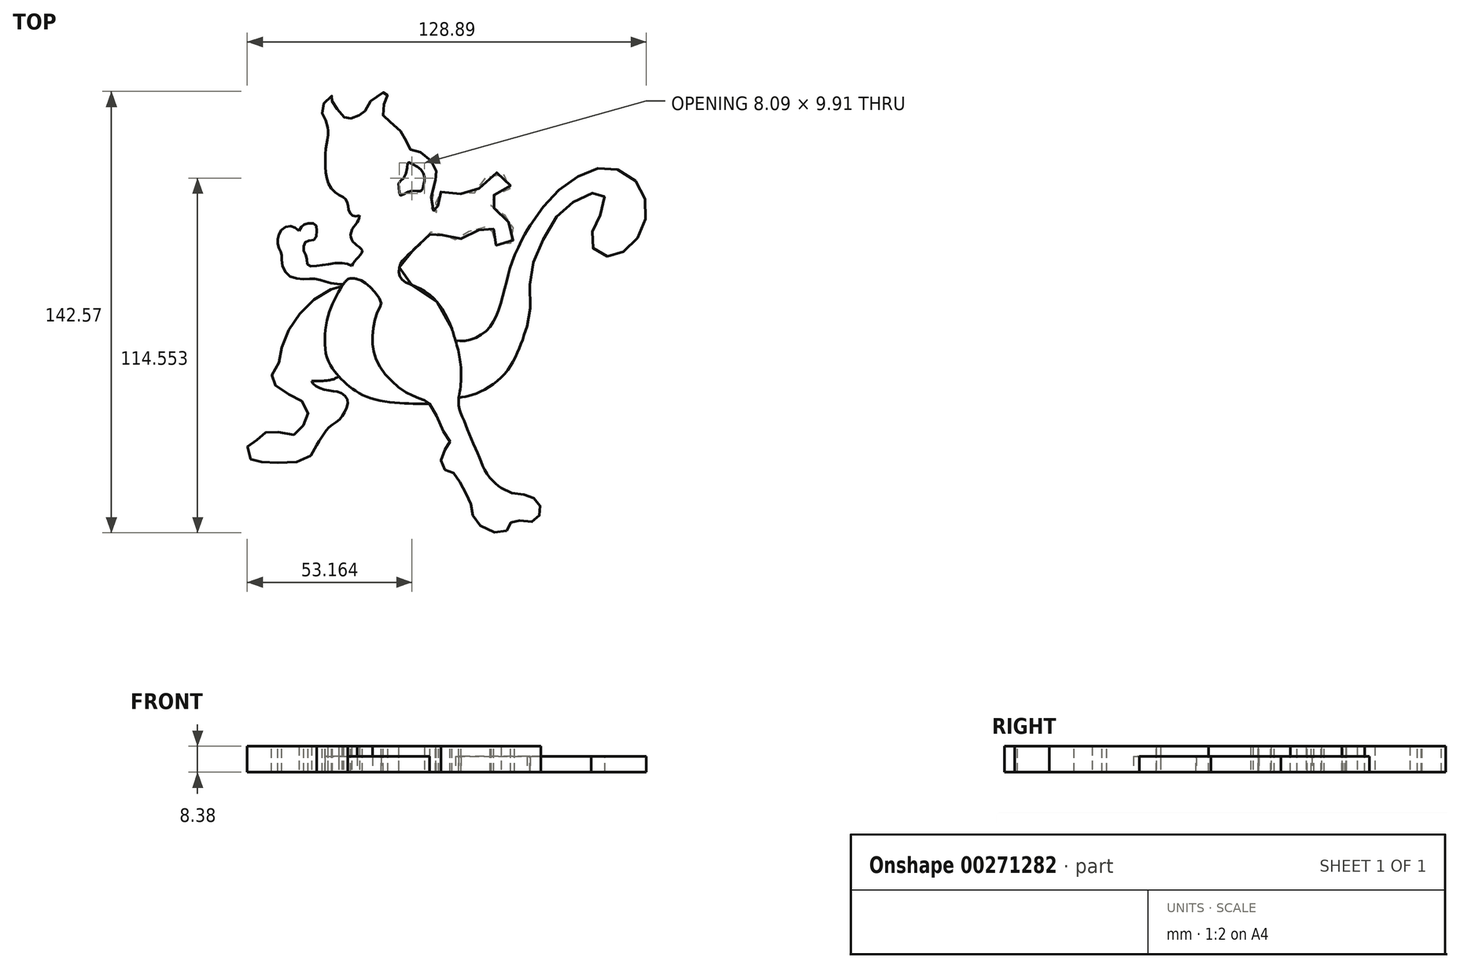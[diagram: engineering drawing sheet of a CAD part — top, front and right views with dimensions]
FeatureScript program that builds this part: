
annotation { "Feature Type Name" : "Feature", "Feature Type Description" : "" }
export const myFeature = defineFeature(function(context is Context, id is Id, definition is map)
    precondition{}
    {
        {
            var Q0;
            Q0=qCreatedBy(makeId("Top.planeOp"),FACE);
            var sketch = newSketch(context, id + "F0", { "sketchPlane" : qUnion([Q0])});
            skFitSpline(sketch, "E0", {"points": [v(-30.68, 33.26) * mm, v(-32.55, 33.12) * mm, v(-33.7, 33.93) * mm, v(-34.3, 35.74) * mm, v(-34.5, 37.15) * mm, v(-35.3, 38.69) * mm, v(-36.98, 39.76) * mm, v(-39.6, 41.77) * mm, v(-41.27, 45.4) * mm, v(-41.74, 50.1) * mm, v(-41.68, 54.72) * mm, v(-41.14, 57.2) * mm, v(-40.87, 60.29) * mm, v(-41, 61.76) * mm], "startDerivative": vector(-29.89, -5.6) * mm, "endDerivative": vector(-3.16, 22.04) * mm});
            skFitSpline(sketch, "E1", {"points": [v(-41, 61.76) * mm, v(-41.17, 62.73) * mm, v(-41.87, 64.35) * mm, v(-42.58, 65.62) * mm, v(-42.68, 67.95) * mm, v(-41.66, 70.39) * mm, v(-39.53, 72) * mm, v(-39.68, 71.35) * mm, v(-39.43, 69.88) * mm, v(-38.31, 68.15) * mm, v(-36.34, 65.92) * mm, v(-34.76, 64.3) * mm, v(-33.44, 64.8) * mm, v(-31.72, 65.72) * mm, v(-29.44, 65.67) * mm, v(-28.78, 68.05) * mm, v(-26.24, 71) * mm, v(-21.98, 73.38) * mm, v(-21.52, 72.72) * mm, v(-22.49, 70.8) * mm, v(-22.9, 68) * mm, v(-22.94, 65.21) * mm, v(-20.91, 63.69) * mm, v(-17.41, 60.44) * mm, v(-15.59, 57.5) * mm, v(-14.77, 54.91) * mm, v(-13, 54.5) * mm, v(-9.24, 52.68) * mm, v(-6.56, 49.33) * mm, v(-5.9, 46.64) * mm, v(-6.17, 44.77) * mm], "startDerivative": vector(-4.63, 41.75) * mm, "endDerivative": vector(1.78, -61.04) * mm});
            skFitSpline(sketch, "E2", {"points": [v(-10.86, 41.22) * mm, v(-13.35, 41.27) * mm, v(-15.9, 40.53) * mm, v(-17.55, 39.84) * mm, v(-17.97, 41.87) * mm, v(-17.97, 43.9) * mm, v(-16.72, 45.15) * mm, v(-15.38, 48.56) * mm, v(-15.06, 50.5) * mm, v(-13.44, 49.9) * mm, v(-11.09, 48.29) * mm, v(-9.93, 46.35) * mm, v(-9.75, 44.36) * mm, v(-10.12, 42.65) * mm, v(-10.86, 41.22) * mm]});
            skFitSpline(sketch, "E3", {"points": [v(-6.17, 44.77) * mm, v(-6.16, 41.94) * mm, v(-6.95, 40.05) * mm, v(-7.82, 38.74) * mm, v(-7.9, 37.04) * mm, v(-7.54, 35.26) * mm, v(-6.56, 34.7) * mm, v(-6.17, 34.08) * mm, v(-5.4, 34.9) * mm, v(-5.12, 35.69) * mm, v(-5.55, 36.6) * mm, v(-6.17, 38.2) * mm, v(-5.6, 39.95) * mm, v(-3.84, 41.22) * mm, v(-1.16, 41.22) * mm, v(1.86, 40.31) * mm, v(4.7, 40.3) * mm, v(7.28, 41.22) * mm, v(9.35, 44.77) * mm, v(12.66, 47.12) * mm, v(15.97, 46.6) * mm, v(17.73, 44.77) * mm, v(17.63, 41.22) * mm, v(15.25, 39.88) * mm, v(12.14, 39.78) * mm, v(11.52, 38.23) * mm, v(11.73, 36.57) * mm, v(13.7, 35.12) * mm, v(16.28, 33.26) * mm, v(17.63, 30.99) * mm, v(18.97, 29.02) * mm, v(19.18, 25.92) * mm, v(17.52, 23.95) * mm, v(15.56, 23.23) * mm, v(12.87, 24.06) * mm, v(11.83, 26.44) * mm, v(12.35, 28.4) * mm, v(12.56, 29.64) * mm, v(10.18, 29.75) * mm, v(8.21, 28.71) * mm, v(4.8, 28.2) * mm, v(2.94, 26.33) * mm, v(0, 25.4) * mm, v(-3.06, 26.02) * mm, v(-3.78, 27.06) * mm, v(-6.17, 28.3) * mm, v(-7.4, 28.6) * mm, v(-8.34, 26.33) * mm, v(-10.1, 24.88) * mm, v(-13.5, 21.99) * mm, v(-16.61, 18.99) * mm, v(-17.95, 16.2) * mm, v(-17.23, 12.89) * mm, v(-13.4, 10.71) * mm, v(-8.13, 7.82) * mm, v(-3.37, 2.03) * mm, v(-0.89, -3.25) * mm], "startDerivative": vector(-12.96, -156.97) * mm, "endDerivative": vector(78.88, -192.56) * mm});
            skFitSpline(sketch, "E4", {"points": [v(-0.89, -3.25) * mm, v(0.76, -8.75) * mm, v(1.86, -13.9) * mm, v(2.03, -20.85) * mm, v(1.35, -25.59) * mm, v(1.52, -29.06) * mm, v(3.04, -32.95) * mm, v(5.07, -38.2) * mm, v(7.7, -44.12) * mm, v(9.56, -48.6) * mm, v(12.6, -52.75) * mm, v(15.06, -54.7) * mm], "startDerivative": vector(17.8, -57.58) * mm, "endDerivative": vector(33.46, -23) * mm});
            skFitSpline(sketch, "E5", {"points": [v(15.06, -54.7) * mm, v(19.22, -56.54) * mm, v(23.7, -57.1) * mm, v(26.51, -58.79) * mm, v(27.91, -61.73) * mm, v(26.51, -64.67) * mm, v(23.57, -65.8) * mm, v(18.8, -65.1) * mm, v(17.68, -67.47) * mm, v(15.06, -69.16) * mm, v(8.3, -66.91) * mm, v(5.63, -62.57) * mm, v(4.93, -58.65) * mm, v(2.27, -54.15) * mm, v(0, -50.1) * mm, v(-2.5, -49.26) * mm, v(-4.32, -46.6) * mm, v(-3.34, -42.67) * mm, v(-1.52, -39.87) * mm, v(-3.9, -35.94) * mm, v(-7.4, -28.23) * mm, v(-10.77, -26) * mm, v(-15.81, -23.75) * mm, v(-22.68, -17.58) * mm, v(-26.18, -10.44) * mm, v(-26.32, -3.57) * mm, v(-24.64, 2.88) * mm, v(-23.66, 4.98) * mm, v(-26.18, 9.04) * mm, v(-29.34, 11.93) * mm, v(-31.48, 12.79) * mm], "startDerivative": vector(118.87, -67.55) * mm, "endDerivative": vector(-88.54, 26.32) * mm});
            skFitSpline(sketch, "E6", {"points": [v(-31.48, 12.79) * mm, v(-32.81, 13) * mm, v(-34.34, 12.79) * mm, v(-35.67, 11.5) * mm, v(-36.87, 9.72) * mm, v(-38.76, 6.22) * mm, v(-40.54, 2.03) * mm, v(-41.65, -3.06) * mm, v(-41.87, -8.6) * mm, v(-40.99, -13.24) * mm, v(-39.1, -16.56) * mm, v(-37.45, -18.66) * mm], "startDerivative": vector(-21.94, 4.47) * mm, "endDerivative": vector(19.73, -23.84) * mm});
            skFitSpline(sketch, "E7", {"points": [v(-37.45, -18.66) * mm, v(-39.44, -19.66) * mm, v(-42.87, -20.1) * mm, v(-46.19, -20.1) * mm], "startDerivative": vector(-6.27, -3.9) * mm, "endDerivative": vector(-9.2, 0.16) * mm});
            skFitSpline(sketch, "E8", {"points": [v(-46.19, -20.1) * mm, v(-44.75, -21.87) * mm, v(-40.77, -23.2) * mm, v(-37.45, -23.75) * mm, v(-34.68, -25.96) * mm, v(-35.23, -29.62) * mm, v(-37.45, -32.82) * mm, v(-40.43, -35.04) * mm, v(-42.65, -37.8) * mm, v(-44.53, -40.8) * mm], "startDerivative": vector(12.03, -21.23) * mm, "endDerivative": vector(-16.64, -26.85) * mm});
            skFitSpline(sketch, "E9", {"points": [v(-44.53, -40.8) * mm, v(-46.19, -43.92) * mm, v(-51.06, -46.33) * mm, v(-59.38, -46.45) * mm, v(-63.96, -46.1) * mm, v(-66.25, -44.88) * mm, v(-66.61, -40.8) * mm, v(-63.84, -39.22) * mm, v(-61.43, -37.05) * mm, v(-58.66, -36.2) * mm, v(-52.38, -37.65) * mm, v(-49.37, -35.12) * mm, v(-47.32, -31.38) * mm, v(-48.77, -27.16) * mm, v(-52.87, -24.74) * mm, v(-58.05, -21.37) * mm, v(-59.14, -18.66) * mm, v(-56.97, -14.73) * mm, v(-55.88, -9.3) * mm, v(-52.14, -1.35) * mm, v(-46.19, 5.53) * mm, v(-38.76, 9.99) * mm, v(-36.42, 10.44) * mm], "startDerivative": vector(-31.3, -84.68) * mm, "endDerivative": vector(62.81, 4.36) * mm});
            skFitSpline(sketch, "E10", {"points": [v(-35.94, 11.12) * mm, v(-40.71, 11.69) * mm, v(-44.53, 12.79) * mm, v(-48.52, 12.79) * mm, v(-54.02, 14.3) * mm, v(-55.88, 18.91) * mm, v(-55.88, 21.08) * mm, v(-56.87, 23.24) * mm, v(-57.07, 25.99) * mm, v(-55.88, 28.74) * mm, v(-52.87, 29.92) * mm, v(-50.29, 28.35) * mm], "startDerivative": vector(-46.56, 2.74) * mm, "endDerivative": vector(28.5, -25.95) * mm});
            skFitSpline(sketch, "E11", {"points": [v(-50.29, 28.35) * mm, v(-49.1, 30.11) * mm, v(-47.54, 30.7) * mm, v(-45.1, 30.6) * mm, v(-44.53, 28.35) * mm, v(-45.1, 25.7) * mm, v(-47.63, 25.1) * mm, v(-48.62, 24.02) * mm, v(-48.62, 21.57) * mm, v(-47.83, 19.8) * mm, v(-47.34, 17.24) * mm, v(-44.53, 17.05) * mm, v(-40.54, 17.64) * mm, v(-35.67, 17.93) * mm, v(-33.3, 17.05) * mm], "startDerivative": vector(16.53, 31.63) * mm, "endDerivative": vector(29.4, -15.7) * mm});
            skFitSpline(sketch, "E12", {"points": [v(-33.3, 17.05) * mm, v(-31.48, 19.5) * mm, v(-29.85, 21.86) * mm, v(-31.48, 23.63) * mm, v(-33.3, 25.6) * mm, v(-33.3, 28.35) * mm, v(-31.48, 31.1) * mm, v(-30.68, 33.26) * mm], "startDerivative": vector(10.56, 16.17) * mm, "endDerivative": vector(4.23, 16.47) * mm});
            skFitSpline(sketch, "E13", {"points": [v(-37.45, -18.66) * mm, v(-32.93, -22.69) * mm, v(-25.97, -26.08) * mm, v(-15.78, -27.39) * mm, v(-8.08, -27.46) * mm], "startDerivative": vector(19.26, -19.05) * mm, "endDerivative": vector(29.6, 0.2) * mm});
            skFitSpline(sketch, "E14", {"points": [v(0.28, -7.09) * mm, v(3.5, -7.14) * mm, v(8.3, -5.35) * mm, v(12.06, -1.78) * mm, v(14.4, 3.4) * mm, v(16.67, 11.67) * mm, v(18.55, 18.26) * mm, v(22.12, 26.25) * mm, v(24.38, 30.2) * mm], "startDerivative": vector(33.02, -3.4) * mm, "endDerivative": vector(19.22, 31.73) * mm});
            skFitSpline(sketch, "E15", {"points": [v(24.38, 30.2) * mm, v(29.66, 37.44) * mm, v(36.73, 43.93) * mm, v(44.47, 48.04) * mm, v(51.3, 48.5) * mm, v(58.26, 44.62) * mm, v(61.56, 38.24) * mm, v(61.45, 31.17) * mm, v(57.92, 24.57) * mm, v(52.9, 20.8) * mm, v(48.12, 20.35) * mm, v(44.47, 23.2) * mm, v(44.59, 28.33) * mm, v(47.1, 33.57) * mm, v(48.35, 39.6) * mm, v(45.95, 40.86) * mm, v(39.35, 38.24) * mm, v(32.85, 32.77) * mm, v(26.93, 22.06) * mm, v(24.38, 13.17) * mm, v(24.38, 3.37) * mm, v(23.4, -2.44) * mm], "startDerivative": vector(92.43, 137.98) * mm, "endDerivative": vector(-30.33, -122.9) * mm});
            skFitSpline(sketch, "E16", {"points": [v(23.4, -2.44) * mm, v(20.24, -11.1) * mm, v(14.64, -19.42) * mm, v(6.31, -24.41) * mm, v(1.35, -25.59) * mm], "startDerivative": vector(-10.7, -33.1) * mm, "endDerivative": vector(-23.69, -3.85) * mm});
            skSolve(sketch);
        }
        {
            var Q0;
            Q0=makeQuery(id+"F0.imprint","IMPRINT",FACE,{"disambiguationData":[TD([[makeQuery(id+"F0.imprint","IMPRINT",EDGE,{"derivedFrom":sQuery(id+"F0.wireOp",EDGE,"E0")}),-1.0]])]});
            var Q1;
            {var subQ0=sQuery(id+"F0.wireOp",EDGE,"E7");Q1=makeQuery(id+"F0.imprint","IMPRINT",FACE,{"disambiguationData":[TD([[makeQuery(id+"F0.imprint","IMPRINT",EDGE,{"derivedFrom":subQ0}),-1.0]])]});}
            extrude(context, id + "F1", {"entities" : qUnion([Q0, Q1]), "depth" : 8.38 * mm});
        }
        {
            var Q0;
            {var subQ0=sQuery(id+"F0.wireOp",EDGE,"E13");Q0=makeQuery(id+"F0.imprint","IMPRINT",FACE,{"disambiguationData":[TD([[makeQuery(id+"F0.imprint","IMPRINT",EDGE,{"derivedFrom":subQ0}),1.0]])]});}
            var Q1;
            {var subQ0=sQuery(id+"F0.wireOp",EDGE,"E14");Q1=makeQuery(id+"F0.imprint","IMPRINT",FACE,{"disambiguationData":[TD([[makeQuery(id+"F0.imprint","IMPRINT",EDGE,{"derivedFrom":subQ0}),-1.0]])]});}
            extrude(context, id + "F2", {"entities" : qUnion([Q0, Q1]), "depth" : 5.08 * mm});
        }
    });
